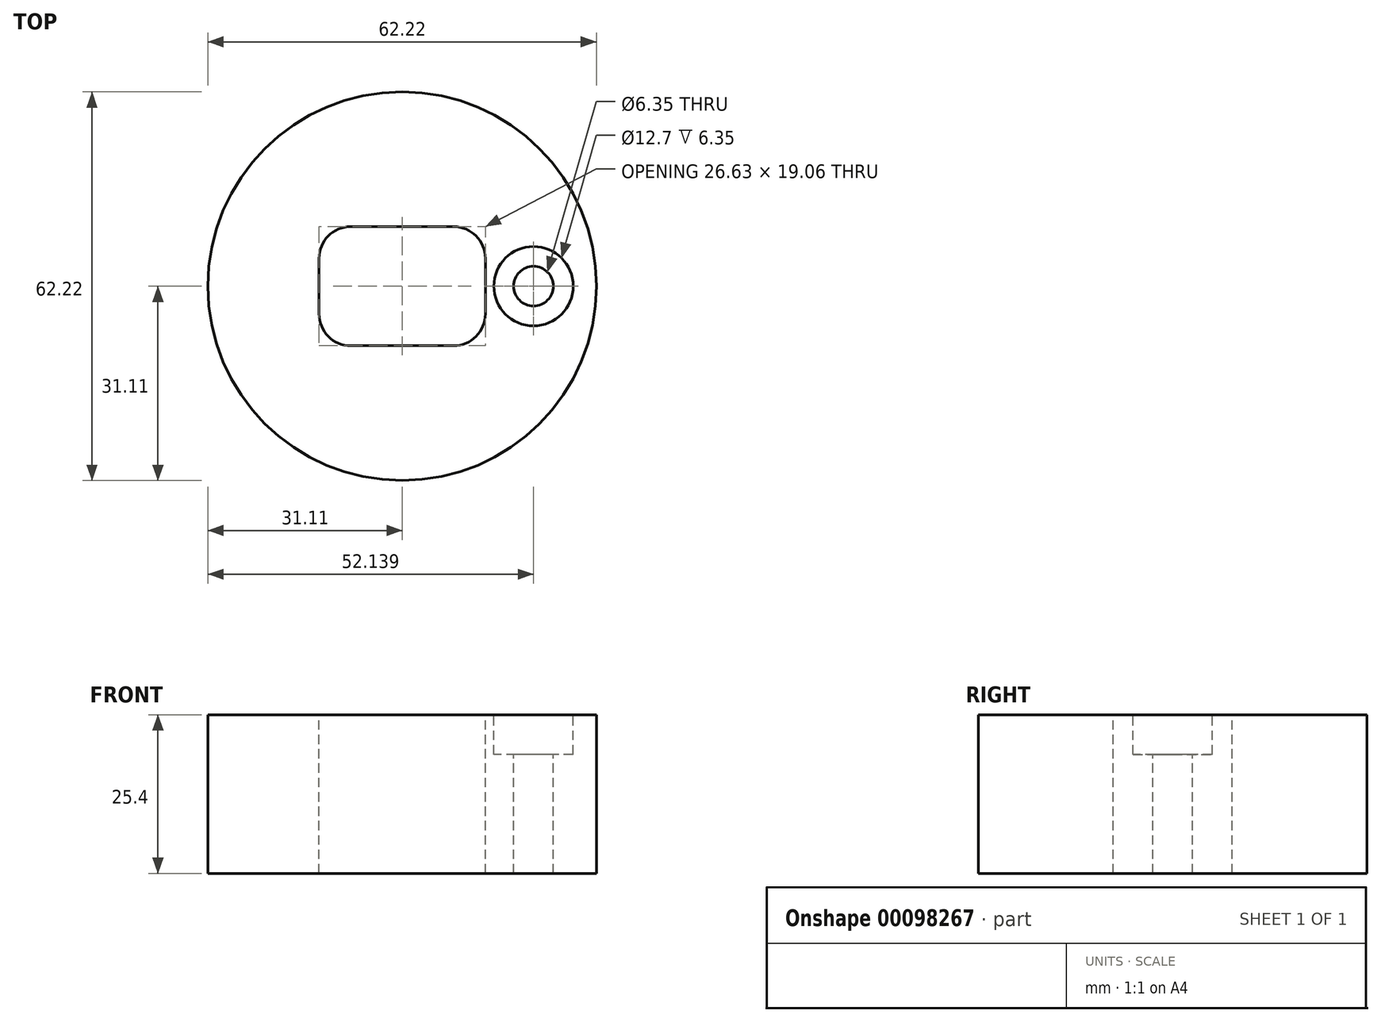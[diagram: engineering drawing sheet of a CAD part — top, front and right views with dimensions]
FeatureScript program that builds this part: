
annotation { "Feature Type Name" : "Feature", "Feature Type Description" : "" }
export const myFeature = defineFeature(function(context is Context, id is Id, definition is map)
    precondition{}
    {
        {
            var Q0;
            Q0=qCreatedBy(makeId("Top.planeOp"),FACE);
            var sketch = newSketch(context, id + "F0", { "sketchPlane" : qUnion([Q0])});
            skCircle(sketch, "E0", {"center": v(0, 0) * mm, "radius": 31.1 * mm});
            skSolve(sketch);
        }
        {
            var Q0;
            Q0 = qSketchRegion(id + "F0", true);
            extrude(context, id + "F1", {"entities" : qUnion([Q0]), "depth" : 25.4 * mm});
        }
        {
            var Q0;
            Q0=makeQuery(id+"F1.opExtrude","CAP_FACE",FACE,{"disambiguationData":[OSD([sQuery(id+"F0.wireOp",EDGE,"E0")])],"isStart":false});
            var sketch = newSketch(context, id + "F2", { "sketchPlane" : qUnion([Q0])});
            skLineSegment(sketch, "E1.bottom", {"start": v(13.31, 9.53) * mm, "end": v(-13.31, 9.53) * mm});
            skLineSegment(sketch, "E1.top", {"start": v(13.31, -9.53) * mm, "end": v(-13.31, -9.53) * mm});
            skLineSegment(sketch, "E1.left", {"start": v(13.31, 9.53) * mm, "end": v(13.31, -9.53) * mm});
            skLineSegment(sketch, "E1.right", {"start": v(-13.31, 9.53) * mm, "end": v(-13.31, -9.53) * mm});
            skPoint(sketch, "E1.middle", {"position": v(0, 0) * mm});
            skSolve(sketch);
        }
        {
            var Q0;
            Q0=makeQuery(id+"F2.imprint","IMPRINT",FACE,{"disambiguationData":[TD([[makeQuery(id+"F2.imprint","IMPRINT",EDGE,{"derivedFrom":sQuery(id+"F2.wireOp",EDGE,"E1.bottom")}),1.0]])]});
            extrude(context, id + "F3", {"entities" : qUnion([Q0]), "operationType" : NewBodyOperationType.REMOVE, "oppositeDirection" : true, "depth" : 25.4 * mm});
        }
        {
            var Q0;
            Q0=makeQuery(id+"F3.boolean.opBoolean","COPY",EDGE,{"derivedFrom":makeQuery(id+"F3.opExtrude","SWEPT_EDGE",EDGE,{"disambiguationData":[OSD([sQuery(id+"F2.wireOp",EDGE,"E1.bottom"),sQuery(id+"F2.wireOp",EDGE,"E1.right")])]})});
            var Q1;
            Q1=makeQuery(id+"F3.boolean.opBoolean","COPY",EDGE,{"derivedFrom":makeQuery(id+"F3.opExtrude","SWEPT_EDGE",EDGE,{"disambiguationData":[OSD([sQuery(id+"F2.wireOp",EDGE,"E1.top"),sQuery(id+"F2.wireOp",EDGE,"E1.right")])]})});
            var Q2;
            Q2=makeQuery(id+"F3.boolean.opBoolean","COPY",EDGE,{"derivedFrom":makeQuery(id+"F3.opExtrude","SWEPT_EDGE",EDGE,{"disambiguationData":[OSD([sQuery(id+"F2.wireOp",EDGE,"E1.bottom"),sQuery(id+"F2.wireOp",EDGE,"E1.left")])]})});
            var Q3;
            Q3=makeQuery(id+"F3.boolean.opBoolean","COPY",EDGE,{"derivedFrom":makeQuery(id+"F3.opExtrude","SWEPT_EDGE",EDGE,{"disambiguationData":[OSD([sQuery(id+"F2.wireOp",EDGE,"E1.top"),sQuery(id+"F2.wireOp",EDGE,"E1.left")])]})});
            fillet(context, id + "F4", {"entities" : qUnion([Q0, Q1, Q2, Q3]), "radius" : 5.08 * mm, "tangentPropagation" : true, "allowEdgeOverflow" : false});
        }
        {
            var Q0;
            Q0=makeQuery(id+"F1.opExtrude","CAP_FACE",FACE,{"disambiguationData":[OSD([sQuery(id+"F0.wireOp",EDGE,"E0")])],"isStart":false});
            var sketch = newSketch(context, id + "F5", { "sketchPlane" : qUnion([Q0])});
            skPoint(sketch, "E2", {"position": v(21.03, 0) * mm});
            skPoint(sketch, "E2.positionSnap0", {"position": v(13.31, 0) * mm});
            skSolve(sketch);
        }
        {
            var Q0;
            Q0=sQuery(id+"F5.wireOp",VERTEX,"E2");
            var Q1;
            Q1=makeQuery(id+"F1.opExtrude","SWEPT_BODY",BODY,{"disambiguationData":[OSD([sQuery(id+"F0.wireOp",EDGE,"E0")])]});
            hole(context, id + "F6", {"style" : HoleStyle.C_BORE, "endStyle" : HoleEndStyle.THROUGH, "holeDiameter" : 6.35 * mm, "cBoreDiameter" : 12.7 * mm, "cBoreDepth" : 6.35 * mm, "startFromSketch" : true, "locations" : qUnion([Q0]), "scope" : qUnion([Q1]), "isTappedThrough" : true});
        }
    });
